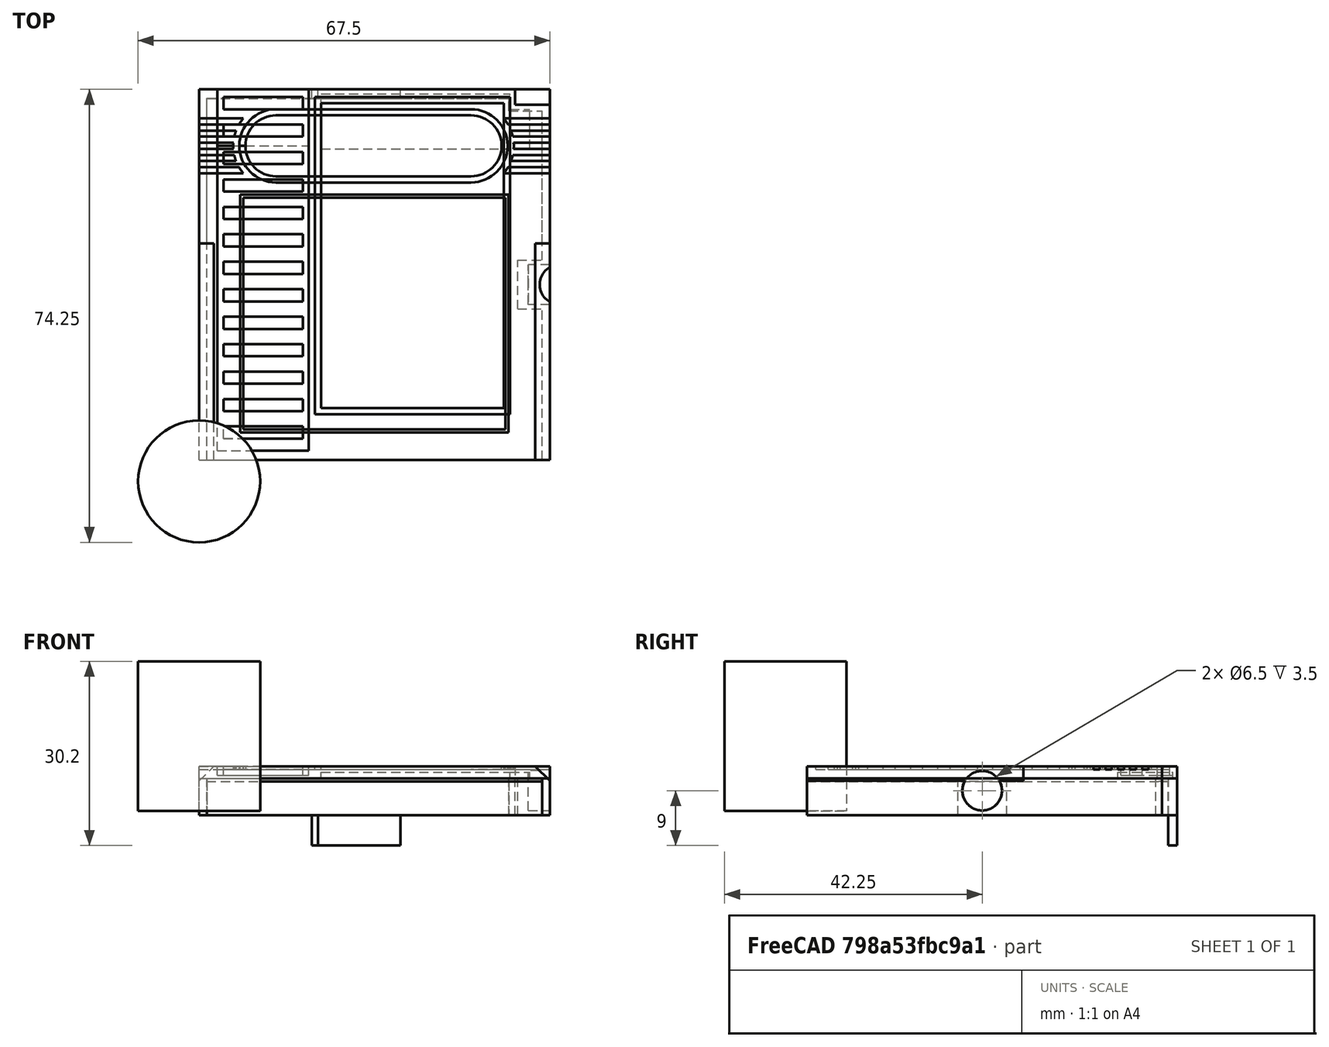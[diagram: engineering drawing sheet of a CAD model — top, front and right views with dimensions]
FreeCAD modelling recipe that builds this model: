
FCSTD DOCUMENT  (FreeCAD 1.0R39109 (Git))
Label: gbc_gameboy_cart_cover_nes
License: All rights reserved
LicenseURL: http://en.wikipedia.org/wiki/All_rights_reserved
objects: Part::Box×52, Part::Cut×17, Part::MultiFuse×13, Part::Cylinder×9, Part::Chamfer×2
note: 93 computed .brp shape members not serialized (recipe doc carries the construction recipe); baked Part::Feature solids carry a one-line shape summary decoded from their .brp

FEATURE [Part::Box] Box  label="Cube(outer_base)"
  AttacherType = Attacher::AttachEngine3D
  Height = 6
  Length = 57.5
  Placement = pos=(0,3.5,-0.7) rot=(0,0,1;0rad)
  Width = 60.75
FEATURE [Part::Box] Box001  label="Cube(corner_inner)"
  AttacherType = Attacher::AttachEngine3D
  Height = 6
  Length = 5.7
  Placement = pos=(51.8,61.75,-0.7) rot=(0,0,1;0rad)
  Width = 2.5
FEATURE [Part::Box] Box002  label="Cube(inner_base)"
  AttacherType = Attacher::AttachEngine3D
  Height = 6
  Length = 55
  Placement = pos=(1.25,0,-0.7) rot=(0,0,1;0rad)
  Width = 62.8
FEATURE [Part::Box] Box003  label="Cube(corner_outer)"
  AttacherType = Attacher::AttachEngine3D
  Height = 6
  Length = 6.2
  Placement = pos=(50.8,60.75,-0.7) rot=(0,0,1;0rad)
  Width = 3.5
FEATURE [Part::Box] Box007  label="Cube(top_cover_top_half)"
  AttacherType = Attacher::AttachEngine3D
  Height = 8
  Length = 57.5
  Placement = pos=(0,39,-0.7) rot=(0,0,1;0rad)
  Width = 25.25
FEATURE [Part::Box] Box008  label="Cube001(top_cover_bottom_half)"
  AttacherType = Attacher::AttachEngine3D
  Height = 8
  Length = 57.5
  Placement = pos=(0,3.5,-0.7) rot=(0,0,1;0rad)
  Width = 35.5
FEATURE [Part::Box] Box010  label="Cube(top_corner_cut)"
  AttacherType = Attacher::AttachEngine3D
  Height = 10
  Length = 10
  Placement = pos=(51.8,61.75,-0.7) rot=(0,0,1;0rad)
  Width = 10
FEATURE [Part::Cut] Cut006
  Base = -> Box007
  Tool = -> Box010
FEATURE [Part::Box] Box017  label="Cube(game_lable_inner)"
  AttacherType = Attacher::AttachEngine3D
  Height = 0.5
  Length = 30
  Placement = pos=(20,12,6.8) rot=(0,0,1;0rad)
  Width = 50
FEATURE [Part::Box] Box018  label="Cube(cube_strips)"
  AttacherType = Attacher::AttachEngine3D
  Height = 0.5
  Length = 15
  Placement = pos=(3,5,6.8) rot=(0,0,1;0rad)
  Width = 53
FEATURE [Part::Box] Box019  label="Cube(cube_strip_top)"
  AttacherType = Attacher::AttachEngine3D
  Height = 1.5
  Length = 15
  Placement = pos=(3,55,5.8) rot=(0,0,1;0rad)
  Width = 9.25
FEATURE [Part::Box] Box020  label="Cube(ladders)"
  AttacherType = Attacher::AttachEngine3D
  Height = 1
  Length = 13
  Placement = pos=(4,7,6.3) rot=(0,0,1;0rad)
  Width = 2
FEATURE [Part::Box] Box021  label="Cube(ladders)001"
  AttacherType = Attacher::AttachEngine3D
  Height = 1
  Length = 13
  Placement = pos=(4,11.5,6.3) rot=(0,0,1;0rad)
  Width = 2
FEATURE [Part::Box] Box022  label="Cube(ladders)002"
  AttacherType = Attacher::AttachEngine3D
  Height = 1
  Length = 13
  Placement = pos=(4,16,6.3) rot=(0,0,1;0rad)
  Width = 2
FEATURE [Part::Box] Box023  label="Cube(ladders)003"
  AttacherType = Attacher::AttachEngine3D
  Height = 1
  Length = 13
  Placement = pos=(4,20.5,6.3) rot=(0,0,1;0rad)
  Width = 2
FEATURE [Part::Box] Box024  label="Cube(ladders)004"
  AttacherType = Attacher::AttachEngine3D
  Height = 1
  Length = 13
  Placement = pos=(4,25,6.3) rot=(0,0,1;0rad)
  Width = 2
FEATURE [Part::Box] Box025  label="Cube(ladders)005"
  AttacherType = Attacher::AttachEngine3D
  Height = 1
  Length = 13
  Placement = pos=(4,29.5,6.3) rot=(0,0,1;0rad)
  Width = 2
FEATURE [Part::Box] Box029  label="Cube(cube_strip_top_outer)"
  AttacherType = Attacher::AttachEngine3D
  Height = 1.5
  Length = 17
  Placement = pos=(2,55,5.8) rot=(0,0,1;0rad)
  Width = 9.25
FEATURE [Part::MultiFuse] Fusion003
  Shapes = -> [Cut006,Box029]
FEATURE [Part::Box] Box030  label="Cube(ladders)009"
  AttacherType = Attacher::AttachEngine3D
  Height = 1
  Length = 13
  Placement = pos=(4,34,6.3) rot=(0,0,1;0rad)
  Width = 2
FEATURE [Part::Box] Box031  label="Cube(ladders)010"
  AttacherType = Attacher::AttachEngine3D
  Height = 1
  Length = 13
  Placement = pos=(4,38.5,6.3) rot=(0,0,1;0rad)
  Width = 2
FEATURE [Part::Box] Box032  label="Cube(ladders)011"
  AttacherType = Attacher::AttachEngine3D
  Height = 1
  Length = 13
  Placement = pos=(4,43,6.3) rot=(0,0,1;0rad)
  Width = 2
FEATURE [Part::Box] Box034  label="Cube(ladders)013"
  AttacherType = Attacher::AttachEngine3D
  Height = 1
  Length = 13
  Placement = pos=(4,47.5,6.3) rot=(0,0,1;0rad)
  Width = 2
FEATURE [Part::Box] Box035  label="Cube(ladders)014"
  AttacherType = Attacher::AttachEngine3D
  Height = 1
  Length = 13
  Placement = pos=(4,52,6.3) rot=(0,0,1;0rad)
  Width = 2
FEATURE [Part::Box] Box038  label="Cube(ladders)017"
  AttacherType = Attacher::AttachEngine3D
  Height = 1.5
  Length = 13
  Placement = pos=(4,56.5,5.8) rot=(0,0,1;0rad)
  Width = 2
FEATURE [Part::Box] Box040  label="Cube(ladders)019"
  AttacherType = Attacher::AttachEngine3D
  Height = 1.5
  Length = 13
  Placement = pos=(4,61,5.8) rot=(0,0,1;0rad)
  Width = 2
FEATURE [Part::Box] Box041  label="Cube(game_lable_outer)"
  AttacherType = Attacher::AttachEngine3D
  Height = 0.5
  Length = 32
  Placement = pos=(19,11,6.8) rot=(0,0,1;0rad)
  Width = 52
FEATURE [Part::MultiFuse] Fusion006  label="Fusion006(ladder)"
  Shapes = -> [Box040,Box038,Box035,Box034,Box032,Box025,Box022,Box021,Box024,Box031,Box023,Box030,Box020]
FEATURE [Part::Box] Box057  label="Cube"
  AttacherType = Attacher::AttachEngine3D
  Height = 1
  Length = 31
  Placement = pos=(20,54.5,5.3) rot=(0,0,1;0rad)
  Width = 9
FEATURE [Part::Box] Box058  label="Cube001"
  AttacherType = Attacher::AttachEngine3D
  Height = 1
  Length = 3.25
  Placement = pos=(51,54.5,5.3) rot=(0,0,1;0rad)
  Width = 6.5
FEATURE [Part::MultiFuse] Fusion023  label="Fusion023(front_cutter_top)"
  Shapes = -> [Box058,Box057]
FEATURE [Part::Cylinder] Cylinder005  label="Cylinder(conduit_left)"
  Angle = 360
  AttacherType = Attacher::AttachEngine3D
  FirstAngle = 0
  Height = 24.5
  Radius = 10
  SecondAngle = 0
FEATURE [Part::Box] Box061  label="Cube(outer_base)001"
  AttacherType = Attacher::AttachEngine3D
  Height = 5.5
  Length = 57.5
  Placement = pos=(0,3.5,-0.7) rot=(0,0,1;0rad)
  Width = 60.75
FEATURE [Part::Box] Box062  label="Cube(corner_inner)001"
  AttacherType = Attacher::AttachEngine3D
  Height = 6
  Length = 5.7
  Placement = pos=(51.8,61.75,-0.7) rot=(0,0,1;0rad)
  Width = 2.5
FEATURE [Part::Box] Box063  label="Cube(inner_base)001"
  AttacherType = Attacher::AttachEngine3D
  Height = 5.5
  Length = 55
  Placement = pos=(1.25,0,-0.7) rot=(0,0,1;0rad)
  Width = 62.75
FEATURE [Part::Box] Box064  label="Cube(corner_outer)001"
  AttacherType = Attacher::AttachEngine3D
  Height = 6
  Length = 5.5
  Placement = pos=(50.8,60.75,-0.7) rot=(0,0,1;0rad)
  Width = 3.5
FEATURE [Part::Box] Box065  label="Cube(game_lable_inner)001"
  AttacherType = Attacher::AttachEngine3D
  Height = 0.5
  Length = 43
  Placement = pos=(7.25,8.5,6.8) rot=(0,0,1;0rad)
  Width = 38
FEATURE [Part::Cut] Cut030
  Base = -> Box061
  Tool = -> Box063
FEATURE [Part::MultiFuse] Fusion030
  Shapes = -> [Cut030,Box064]
FEATURE [Part::Cut] Cut031  label="Cut024"
  Base = -> Fusion030
  Tool = -> Box062
FEATURE [Part::Box] Box066  label="Cube(sd_card_cover)"
  AttacherType = Attacher::AttachEngine3D
  Height = 5
  Length = 13.5
  Placement = pos=(19.5,62.75,-5.7) rot=(0,0,1;0rad)
  Width = 1.5
FEATURE [Part::Box] Box067  label="Cube(magnet_black)"
  AttacherType = Attacher::AttachEngine3D
  Height = 6
  Length = 4
  Placement = pos=(52.25,28.25,-0.7) rot=(0,0,1;0rad)
  Width = 8
FEATURE [Part::Cylinder] Cylinder006  label="Cylinder(magnet)"
  Angle = 360
  AttacherType = Attacher::AttachEngine3D
  FirstAngle = 0
  Height = 3.5
  Placement = pos=(54,32.25,3.3) rot=(0,1,0;1.5708rad)
  Radius = 3.25
  SecondAngle = 0
FEATURE [Part::Box] Box068  label="Cube(game_lable_outer)001"
  AttacherType = Attacher::AttachEngine3D
  Height = 0.5
  Length = 44
  Placement = pos=(6.75,8,6.8) rot=(0,0,1;0rad)
  Width = 39
FEATURE [Part::Box] Box069  label="Cube(middle_nintendo_inner)"
  AttacherType = Attacher::AttachEngine3D
  Height = 0.5
  Length = 32
  Placement = pos=(12.6,50,6.8) rot=(0,0,1;0rad)
  Width = 10
FEATURE [Part::Cylinder] Cylinder011  label="Cylinder002(right_nintendo_inner)"
  Angle = 360
  AttacherType = Attacher::AttachEngine3D
  FirstAngle = 0
  Height = 0.5
  Placement = pos=(44.6,55,6.8) rot=(0,0,1;0rad)
  Radius = 5
  SecondAngle = 0
FEATURE [Part::Cylinder] Cylinder010  label="Cylinder001(left_nintendo_inner)"
  Angle = 360
  AttacherType = Attacher::AttachEngine3D
  FirstAngle = 0
  Height = 0.5
  Placement = pos=(12.6,55,6.8) rot=(0,0,1;0rad)
  Radius = 5
  SecondAngle = 0
FEATURE [Part::MultiFuse] Fusion033
  Shapes = -> [Cylinder010,Cylinder011,Box069]
FEATURE [Part::Box] Box070  label="Cube001(top_cover_bottom_half)001"
  AttacherType = Attacher::AttachEngine3D
  Height = 2.5
  Length = 57.5
  Placement = pos=(0,3.5,4.8) rot=(0,0,1;0rad)
  Width = 35.5
FEATURE [Part::Box] Box071  label="Cube(middle_nintendo_outer)"
  AttacherType = Attacher::AttachEngine3D
  Height = 1
  Length = 32
  Placement = pos=(12.6,49,6.8) rot=(0,0,1;0rad)
  Width = 12
FEATURE [Part::Cylinder] Cylinder007  label="Cylinder002(right_nintendo_outer)"
  Angle = 360
  AttacherType = Attacher::AttachEngine3D
  FirstAngle = 0
  Height = 1
  Placement = pos=(44.6,55,6.8) rot=(0,0,1;0rad)
  Radius = 6
  SecondAngle = 0
FEATURE [Part::Cylinder] Cylinder012  label="Cylinder001(left_nintendo_outer)"
  Angle = 360
  AttacherType = Attacher::AttachEngine3D
  FirstAngle = 0
  Height = 1
  Placement = pos=(12.6,55,6.8) rot=(0,0,1;0rad)
  Radius = 6
  SecondAngle = 0
FEATURE [Part::Cylinder] Cylinder008  label="Cylinder001(left_nintendo_fin_cut)"
  Angle = 360
  AttacherType = Attacher::AttachEngine3D
  FirstAngle = 0
  Height = 1
  Placement = pos=(12.6,55,6.8) rot=(0,0,1;0rad)
  Radius = 7
  SecondAngle = 0
FEATURE [Part::Box] Box072  label="Cube001(left_fin_5)"
  AttacherType = Attacher::AttachEngine3D
  Height = 1
  Length = 10
  Placement = pos=(0,52.5,6.8) rot=(0,0,1;0rad)
  Width = 1
FEATURE [Part::Box] Box073  label="Cube003(left_fin_4)"
  AttacherType = Attacher::AttachEngine3D
  Height = 1
  Length = 10
  Placement = pos=(0,56.5,6.8) rot=(0,0,1;0rad)
  Width = 1
FEATURE [Part::Box] Box074  label="Cube004(left_fin_3)"
  AttacherType = Attacher::AttachEngine3D
  Height = 1
  Length = 10
  Placement = pos=(0,58.5,6.8) rot=(0,0,1;0rad)
  Width = 1
FEATURE [Part::Box] Box075  label="Cube002(left_fin_2)"
  AttacherType = Attacher::AttachEngine3D
  Height = 1
  Length = 10
  Placement = pos=(0,54.5,6.8) rot=(0,0,1;0rad)
  Width = 1
FEATURE [Part::Box] Box076  label="Cube(left_fin_1)"
  AttacherType = Attacher::AttachEngine3D
  Height = 1
  Length = 10
  Placement = pos=(0,50.5,6.8) rot=(0,0,1;0rad)
  Width = 1
FEATURE [Part::MultiFuse] Fusion004
  Shapes = -> [Box076,Box075,Box074,Box073,Box072]
FEATURE [Part::Cut] Cut009
  Base = -> Fusion004
  Tool = -> Cylinder008
FEATURE [Part::Cylinder] Cylinder009  label="Cylinder002(right_nintendo_fin_cut)"
  Angle = 360
  AttacherType = Attacher::AttachEngine3D
  FirstAngle = 0
  Height = 1
  Placement = pos=(44.6,55,6.8) rot=(0,0,1;0rad)
  Radius = 7
  SecondAngle = 0
FEATURE [Part::Box] Box077  label="Cube004(right_fin_3)"
  AttacherType = Attacher::AttachEngine3D
  Height = 1
  Length = 10
  Placement = pos=(47.5,58.5,6.8) rot=(0,0,1;0rad)
  Width = 1
FEATURE [Part::Box] Box078  label="Cube003(right_fin_4)"
  AttacherType = Attacher::AttachEngine3D
  Height = 1
  Length = 10
  Placement = pos=(47.5,56.5,6.8) rot=(0,0,1;0rad)
  Width = 1
FEATURE [Part::Box] Box079  label="Cube001(right_fin_5)"
  AttacherType = Attacher::AttachEngine3D
  Height = 1
  Length = 10
  Placement = pos=(47.5,52.5,6.8) rot=(0,0,1;0rad)
  Width = 1
FEATURE [Part::Box] Box080  label="Cube002(right_fin_2)"
  AttacherType = Attacher::AttachEngine3D
  Height = 1
  Length = 10
  Placement = pos=(47.5,54.5,6.8) rot=(0,0,1;0rad)
  Width = 1
FEATURE [Part::Box] Box081  label="Cube(right_fin_1)"
  AttacherType = Attacher::AttachEngine3D
  Height = 1
  Length = 10
  Placement = pos=(47.5,50.5,6.8) rot=(0,0,1;0rad)
  Width = 1
FEATURE [Part::MultiFuse] Fusion034
  Shapes = -> [Box081,Box080,Box079,Box078,Box077]
FEATURE [Part::Cut] Cut032
  Base = -> Fusion034
  Tool = -> Cylinder009
FEATURE [Part::Box] Box082  label="Cube(top_corner_cut)001"
  AttacherType = Attacher::AttachEngine3D
  Height = 10
  Length = 10
  Placement = pos=(51.8,61.75,0) rot=(0,0,1;0rad)
  Width = 10
FEATURE [Part::Box] Box083  label="Cube(top_cover_top_half)001"
  AttacherType = Attacher::AttachEngine3D
  Height = 2.5
  Length = 57.5
  Placement = pos=(0,39,4.8) rot=(0,0,1;0rad)
  Width = 25.25
FEATURE [Part::Cut] Cut033
  Base = -> Box083
  Tool = -> Box082
FEATURE [Part::Cut] Cut010
  Base = -> Cut033
  Tool = -> Cut032
FEATURE [Part::Cut] Cut011
  Base = -> Cut010
  Tool = -> Cut009
FEATURE [Part::Cut] Cut012
  Base = -> Cut011
  Tool = -> Cylinder012
FEATURE [Part::Cut] Cut013
  Base = -> Cut012
  Tool = -> Cylinder007
FEATURE [Part::Cut] Cut014
  Base = -> Cut013
  Tool = -> Box071
FEATURE [Part::Chamfer] Chamfer001
  Base = -> Box070
  EdgeLinks = -> Box070 [Edge2,Edge6]
  Edges = 2 edges r=2.4: [Edge2,Edge6]
FEATURE [Part::MultiFuse] Fusion035
  Shapes = -> [Box067,Chamfer001,Cut031,Fusion033,Cut014]
FEATURE [Part::Cut] Cut034
  Base = -> Fusion035
  Tool = -> Cylinder006
FEATURE [Part::Cut] Cut035
  Base = -> Cut034
  Tool = -> Box068
FEATURE [Part::MultiFuse] Fusion036
  Shapes = -> [Cut035,Box065]
FEATURE [Part::Box] Box084  label="Cube(sd_card_cover)001"
  AttacherType = Attacher::AttachEngine3D
  Height = 5
  Length = 14.5
  Placement = pos=(18.5,62.75,-5.7) rot=(0,0,1;0rad)
  Width = 1.5
FEATURE [Part::Cylinder] Cylinder013  label="Cylinder(magnet)001"
  Angle = 360
  AttacherType = Attacher::AttachEngine3D
  FirstAngle = 0
  Height = 3.5
  Placement = pos=(54,32.25,3.3) rot=(0,1,0;1.5708rad)
  Radius = 3.25
  SecondAngle = 0
FEATURE [Part::Box] Box085  label="Cube(magnet_black)001"
  AttacherType = Attacher::AttachEngine3D
  Height = 6
  Length = 4
  Placement = pos=(52.25,28.25,-0.7) rot=(0,0,1;0rad)
  Width = 8
FEATURE [Part::MultiFuse] Fusion037
  Shapes = -> [Fusion036,Box066]
FEATURE [Part::Chamfer] Chamfer
  Base = -> Box008
  EdgeLinks = -> Box008 [Edge2,Edge6]
  Edges = 2 edges r=2.4: [Edge2,Edge6]
FEATURE [Part::MultiFuse] Fusion
  Shapes = -> [Fusion003,Chamfer]
FEATURE [Part::MultiFuse] Fusion041
  Shapes = -> [Box019,Box018,Box041]
FEATURE [Part::Cut] Cut
  Base = -> Fusion
  Tool = -> Fusion041
FEATURE [Part::Cut] Cut036
  Base = -> Cut
  Tool = -> Box002
FEATURE [Part::Cut] Cut037
  Base = -> Box003
  Tool = -> Box001
FEATURE [Part::MultiFuse] Fusion042
  Shapes = -> [Cut037,Cut036,Box085,Box084,Box017,Fusion006]
FEATURE [Part::Cut] Cut038
  Base = -> Fusion042
  Tool = -> Cylinder013
